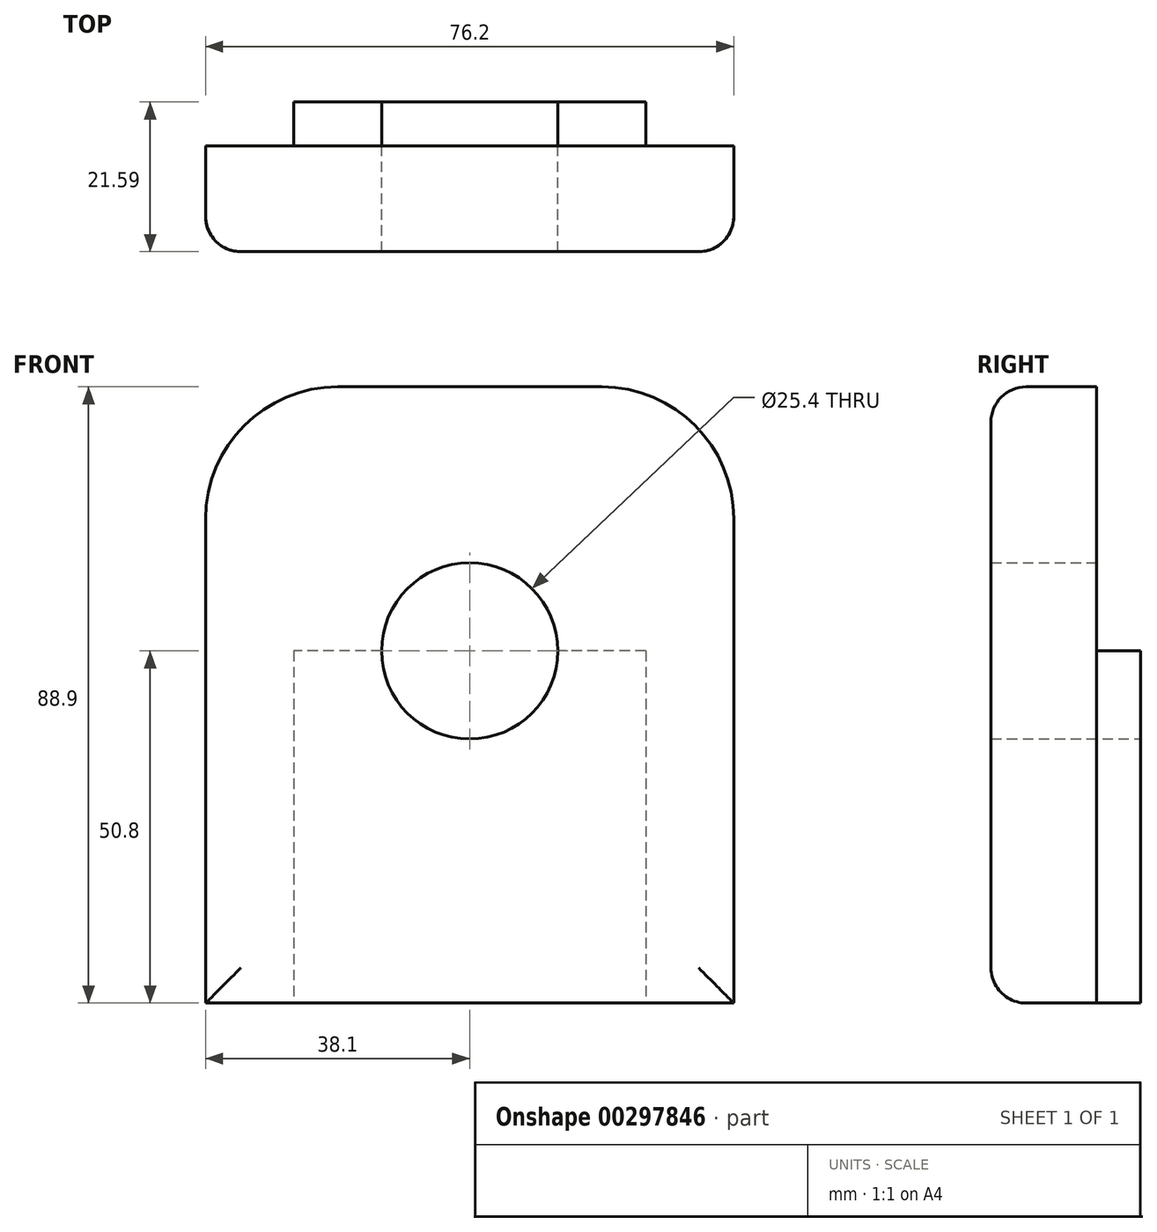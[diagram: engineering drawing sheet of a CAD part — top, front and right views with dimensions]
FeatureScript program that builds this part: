
annotation { "Feature Type Name" : "Feature", "Feature Type Description" : "" }
export const myFeature = defineFeature(function(context is Context, id is Id, definition is map)
    precondition{}
    {
        {
            var Q0;
            Q0=qCreatedBy(makeId("Front.planeOp"),FACE);
            var sketch = newSketch(context, id + "F0", { "sketchPlane" : qUnion([Q0])});
            skLineSegment(sketch, "E0.bottom", {"start": v(-19.05, 38.1) * mm, "end": v(19.05, 38.1) * mm});
            skLineSegment(sketch, "E0.top", {"start": v(-38.1, -50.8) * mm, "end": v(38.1, -50.8) * mm});
            skLineSegment(sketch, "E0.left", {"start": v(-38.1, 19.05) * mm, "end": v(-38.1, -50.8) * mm});
            skLineSegment(sketch, "E0.right", {"start": v(38.1, 19.05) * mm, "end": v(38.1, -50.8) * mm});
            skArc(sketch, "E1", {"start": v(12.7, 0) * mm, "mid": v(0, 12.7) * mm, "end": v(-12.7, 0) * mm, "construction": true});
            skLineSegment(sketch, "E2.bottom", {"start": v(12.7, 0) * mm, "end": v(12.7, 0) * mm});
            skLineSegment(sketch, "E2.top", {"start": v(-12.7, -50.8) * mm, "end": v(12.7, -50.8) * mm, "construction": true});
            skLineSegment(sketch, "E2.left", {"start": v(-12.7, 0) * mm, "end": v(-12.7, -50.8) * mm, "construction": true});
            skLineSegment(sketch, "E2.right", {"start": v(12.7, 0) * mm, "end": v(12.7, -50.8) * mm, "construction": true});
            skCircle(sketch, "E3", {"center": v(0, 0) * mm, "radius": 12.7 * mm});
            skPoint(sketch, "E4.visualSharp", {"position": v(-38.1, 38.1) * mm});
            skArc(sketch, "E4.filletArc", {"start": v(-19.05, 38.1) * mm, "mid": v(-32.52, 32.52) * mm, "end": v(-38.1, 19.05) * mm});
            skPoint(sketch, "E5.visualSharp", {"position": v(38.1, 38.1) * mm});
            skArc(sketch, "E5.filletArc", {"start": v(38.1, 19.05) * mm, "mid": v(32.52, 32.52) * mm, "end": v(19.05, 38.1) * mm});
            skSolve(sketch);
        }
        {
            var Q0;
            Q0=makeQuery(id+"F0.imprint","IMPRINT",FACE,{"disambiguationData":[TD([[makeQuery(id+"F0.imprint","IMPRINT",EDGE,{"derivedFrom":sQuery(id+"F0.wireOp",EDGE,"E0.bottom")}),-1.0]])]});
            extrude(context, id + "F1", {"entities" : qUnion([Q0]), "depth" : 15.24 * mm});
        }
        {
            var Q0;
            Q0=qCreatedBy(makeId("Front.planeOp"),FACE);
            var sketch = newSketch(context, id + "F2", { "sketchPlane" : qUnion([Q0])});
            skPoint(sketch, "E6.orphan", {"position": v(12.7, 0) * mm});
            skPoint(sketch, "E7.orphan", {"position": v(-12.7, 0) * mm});
            skPoint(sketch, "E8.0.end.orphan", {"position": v(12.7, -50.8) * mm});
            skPoint(sketch, "E9.0.end.orphan", {"position": v(-12.7, -50.8) * mm});
            skLineSegment(sketch, "E10.bottom", {"start": v(25.4, 0) * mm, "end": v(12.7, 0) * mm});
            skLineSegment(sketch, "E10.top", {"start": v(25.4, -50.8) * mm, "end": v(-25.4, -50.8) * mm});
            skLineSegment(sketch, "E10.left", {"start": v(25.4, 0) * mm, "end": v(25.4, -50.8) * mm});
            skLineSegment(sketch, "E10.right", {"start": v(-25.4, 0) * mm, "end": v(-25.4, -50.8) * mm});
            skArc(sketch, "E11.0", {"start": v(-12.7, 0) * mm, "mid": v(0, -12.7) * mm, "end": v(12.7, 0) * mm});
            skLineSegment(sketch, "E12.trimOffspring", {"start": v(-12.7, 0) * mm, "end": v(-25.4, 0) * mm});
            skSolve(sketch);
        }
        {
            var Q0;
            Q0 = qSketchRegion(id + "F2", true);
            extrude(context, id + "F3", {"entities" : qUnion([Q0]), "operationType" : NewBodyOperationType.ADD, "oppositeDirection" : true, "depth" : 6.35 * mm});
        }
        {
            var Q0;
            Q0=makeQuery(id+"F1.opExtrude","CAP_EDGE",EDGE,{"disambiguationData":[OSD([sQuery(id+"F0.wireOp",EDGE,"E0.left")])],"isStart":false});
            var Q1;
            Q1=makeQuery(id+"F1.opExtrude","CAP_EDGE",EDGE,{"disambiguationData":[OSD([sQuery(id+"F0.wireOp",EDGE,"E4.filletArc")])],"isStart":false});
            var Q2;
            Q2=makeQuery(id+"F1.opExtrude","CAP_EDGE",EDGE,{"disambiguationData":[OSD([sQuery(id+"F0.wireOp",EDGE,"E0.bottom")])],"isStart":false});
            var Q3;
            Q3=makeQuery(id+"F1.opExtrude","CAP_EDGE",EDGE,{"disambiguationData":[OSD([sQuery(id+"F0.wireOp",EDGE,"E5.filletArc")])],"isStart":false});
            var Q4;
            Q4=makeQuery(id+"F1.opExtrude","CAP_EDGE",EDGE,{"disambiguationData":[OSD([sQuery(id+"F0.wireOp",EDGE,"E0.right")])],"isStart":false});
            var Q5;
            Q5=makeQuery(id+"F1.opExtrude","CAP_EDGE",EDGE,{"disambiguationData":[OSD([sQuery(id+"F0.wireOp",EDGE,"E0.top")])],"isStart":false});
            fillet(context, id + "F4", {"entities" : qUnion([Q0, Q1, Q2, Q3, Q4, Q5]), "radius" : 5.08 * mm, "tangentPropagation" : true, "allowEdgeOverflow" : false});
        }
    });
